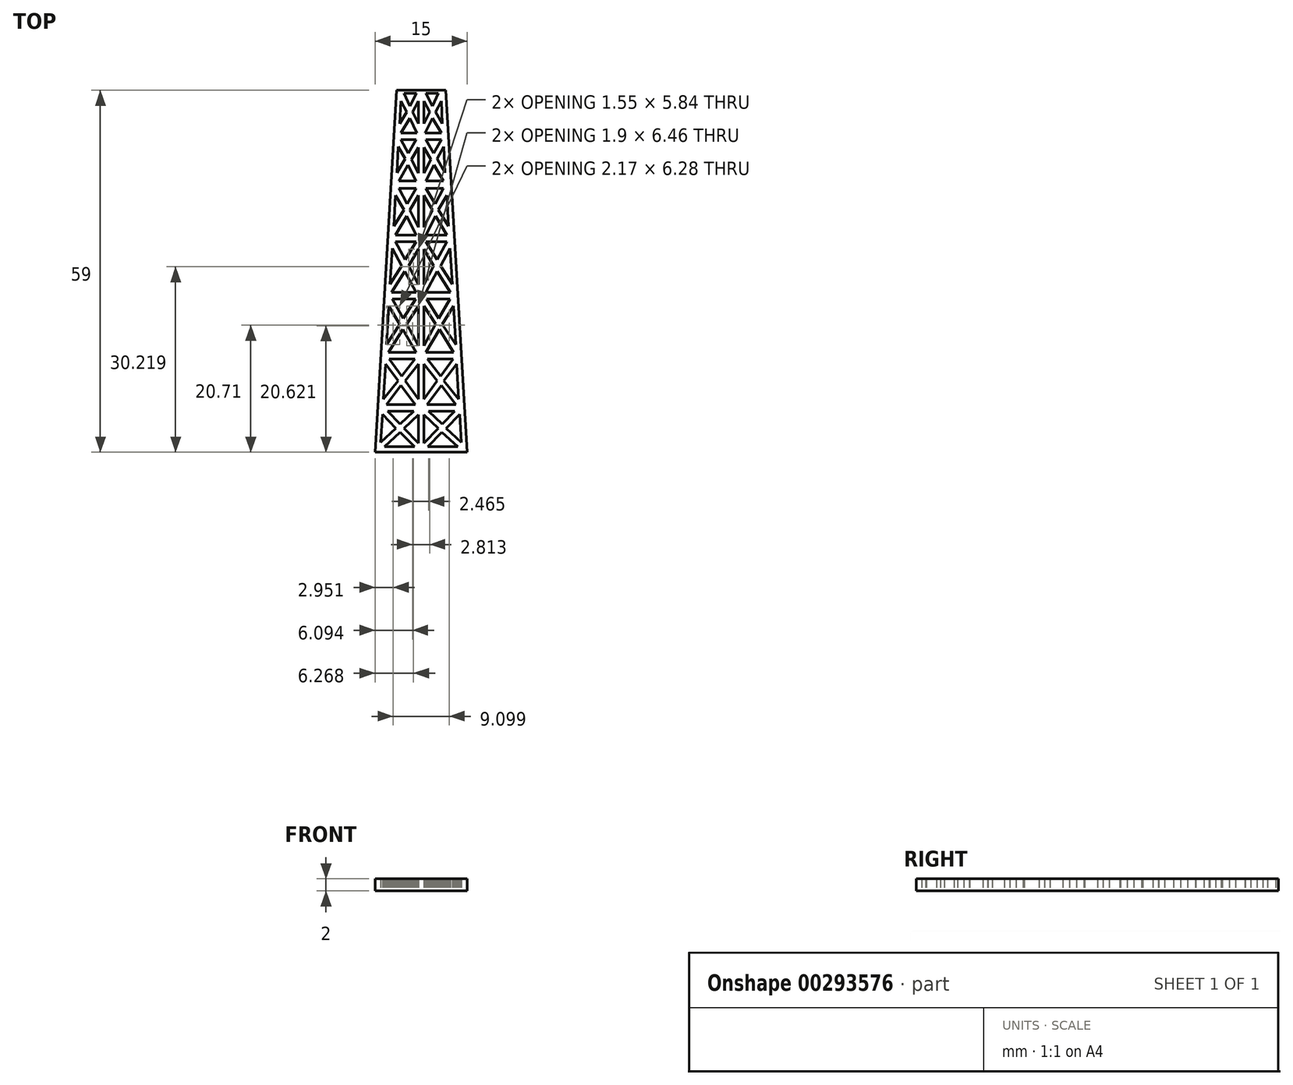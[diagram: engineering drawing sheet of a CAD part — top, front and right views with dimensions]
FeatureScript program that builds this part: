
annotation { "Feature Type Name" : "Feature", "Feature Type Description" : "" }
export const myFeature = defineFeature(function(context is Context, id is Id, definition is map)
    precondition{}
    {
        {
            var Q0;
            Q0=qCreatedBy(makeId("Top.planeOp"),FACE);
            var sketch = newSketch(context, id + "F0", { "sketchPlane" : qUnion([Q0])});
            skLineSegment(sketch, "E0", {"start": v(0, 25.75) * mm, "end": v(-4, 25.75) * mm});
            skLineSegment(sketch, "E1", {"start": v(-4, 25.75) * mm, "end": v(-7.5, -33.25) * mm});
            skLineSegment(sketch, "E2", {"start": v(-7.5, -33.25) * mm, "end": v(0, -33.25) * mm});
            skLineSegment(sketch, "E3", {"start": v(-2.81, 25.28) * mm, "end": v(-0.77, 25.28) * mm});
            skLineSegment(sketch, "E4", {"start": v(-0.77, 25.28) * mm, "end": v(-1.84, 23.18) * mm});
            skLineSegment(sketch, "E5", {"start": v(-1.84, 23.18) * mm, "end": v(-2.81, 25.28) * mm});
            skLineSegment(sketch, "E6", {"start": v(-0.45, 23.96) * mm, "end": v(-1.4, 22.21) * mm});
            skLineSegment(sketch, "E7", {"start": v(-1.4, 22.21) * mm, "end": v(-0.43, 20.28) * mm});
            skLineSegment(sketch, "E8", {"start": v(-0.43, 20.28) * mm, "end": v(-0.45, 23.96) * mm});
            skLineSegment(sketch, "E9", {"start": v(-3.29, 23.96) * mm, "end": v(-3.46, 20.3) * mm});
            skLineSegment(sketch, "E10", {"start": v(-3.46, 20.3) * mm, "end": v(-2.36, 22.21) * mm});
            skLineSegment(sketch, "E11", {"start": v(-2.36, 22.21) * mm, "end": v(-3.29, 23.96) * mm});
            skLineSegment(sketch, "E12", {"start": v(-3.29, 18.76) * mm, "end": v(-0.66, 18.76) * mm});
            skLineSegment(sketch, "E13", {"start": v(-0.66, 18.76) * mm, "end": v(-1.84, 21.21) * mm});
            skLineSegment(sketch, "E14", {"start": v(-1.84, 21.21) * mm, "end": v(-3.29, 18.76) * mm});
            skLineSegment(sketch, "E15", {"start": v(-3.29, 17.7) * mm, "end": v(-0.8, 17.7) * mm});
            skLineSegment(sketch, "E16", {"start": v(-0.8, 17.7) * mm, "end": v(-2.07, 15.47) * mm});
            skLineSegment(sketch, "E17", {"start": v(-2.07, 15.47) * mm, "end": v(-3.29, 17.7) * mm});
            skLineSegment(sketch, "E18", {"start": v(-1.57, 14.45) * mm, "end": v(-0.45, 16.4) * mm});
            skLineSegment(sketch, "E19", {"start": v(-0.45, 16.4) * mm, "end": v(-0.45, 12.22) * mm});
            skLineSegment(sketch, "E20", {"start": v(-0.45, 12.22) * mm, "end": v(-1.57, 14.45) * mm});
            skLineSegment(sketch, "E21", {"start": v(-3.72, 16.56) * mm, "end": v(-3.91, 12.3) * mm});
            skLineSegment(sketch, "E22", {"start": v(-3.91, 12.3) * mm, "end": v(-2.61, 14.57) * mm});
            skLineSegment(sketch, "E23", {"start": v(-2.61, 14.57) * mm, "end": v(-3.72, 16.56) * mm});
            skLineSegment(sketch, "E24", {"start": v(-3.64, 10.94) * mm, "end": v(-0.8, 10.94) * mm});
            skLineSegment(sketch, "E25", {"start": v(-0.8, 10.94) * mm, "end": v(-2.12, 13.58) * mm});
            skLineSegment(sketch, "E26", {"start": v(-2.12, 13.58) * mm, "end": v(-3.64, 10.94) * mm});
            skLineSegment(sketch, "E27", {"start": v(-3.64, 9.76) * mm, "end": v(-0.8, 9.76) * mm});
            skLineSegment(sketch, "E28", {"start": v(-0.8, 9.76) * mm, "end": v(-2.27, 7.2) * mm});
            skLineSegment(sketch, "E29", {"start": v(-2.27, 7.2) * mm, "end": v(-3.64, 9.76) * mm});
            skLineSegment(sketch, "E30", {"start": v(-0.45, 8.61) * mm, "end": v(-1.84, 6.18) * mm});
            skLineSegment(sketch, "E31", {"start": v(-1.84, 6.18) * mm, "end": v(-0.45, 3.41) * mm});
            skLineSegment(sketch, "E32", {"start": v(-0.45, 3.41) * mm, "end": v(-0.45, 8.61) * mm});
            skLineSegment(sketch, "E33", {"start": v(-4.17, 8.61) * mm, "end": v(-2.81, 6.25) * mm});
            skLineSegment(sketch, "E34", {"start": v(-2.81, 6.25) * mm, "end": v(-4.45, 3.62) * mm});
            skLineSegment(sketch, "E35", {"start": v(-4.45, 3.62) * mm, "end": v(-4.17, 8.61) * mm});
            skLineSegment(sketch, "E36", {"start": v(-4.17, 2.13) * mm, "end": v(-0.8, 2.13) * mm});
            skLineSegment(sketch, "E37", {"start": v(-0.8, 2.13) * mm, "end": v(-2.36, 5.25) * mm});
            skLineSegment(sketch, "E38", {"start": v(-2.36, 5.25) * mm, "end": v(-4.17, 2.13) * mm});
            skLineSegment(sketch, "E39", {"start": v(-4.17, 1.08) * mm, "end": v(-0.8, 1.08) * mm});
            skLineSegment(sketch, "E40", {"start": v(-0.8, 1.08) * mm, "end": v(-2.61, -1.83) * mm});
            skLineSegment(sketch, "E41", {"start": v(-2.61, -1.83) * mm, "end": v(-4.17, 1.08) * mm});
            skLineSegment(sketch, "E42", {"start": v(-0.45, -0.11) * mm, "end": v(-2, -2.84) * mm});
            skLineSegment(sketch, "E43", {"start": v(-2, -2.84) * mm, "end": v(-0.45, -5.95) * mm});
            skLineSegment(sketch, "E44", {"start": v(-0.45, -5.95) * mm, "end": v(-0.45, -0.11) * mm});
            skLineSegment(sketch, "E45", {"start": v(-4.71, 0) * mm, "end": v(-5.06, -5.83) * mm});
            skLineSegment(sketch, "E46", {"start": v(-5.06, -5.83) * mm, "end": v(-3.17, -2.84) * mm});
            skLineSegment(sketch, "E47", {"start": v(-3.17, -2.84) * mm, "end": v(-4.71, 0) * mm});
            skLineSegment(sketch, "E48", {"start": v(-4.79, -7.2) * mm, "end": v(-0.8, -7.2) * mm});
            skLineSegment(sketch, "E49", {"start": v(-0.8, -7.2) * mm, "end": v(-2.63, -3.76) * mm});
            skLineSegment(sketch, "E50", {"start": v(-2.63, -3.76) * mm, "end": v(-4.79, -7.2) * mm});
            skLineSegment(sketch, "E51", {"start": v(-4.71, -8.3) * mm, "end": v(-0.9, -8.3) * mm});
            skLineSegment(sketch, "E52", {"start": v(-0.9, -8.3) * mm, "end": v(-2.9, -11.46) * mm});
            skLineSegment(sketch, "E53", {"start": v(-2.9, -11.46) * mm, "end": v(-4.71, -8.3) * mm});
            skLineSegment(sketch, "E54", {"start": v(-0.45, -9.4) * mm, "end": v(-2.36, -12.36) * mm});
            skLineSegment(sketch, "E55", {"start": v(-2.36, -12.36) * mm, "end": v(-0.45, -15.86) * mm});
            skLineSegment(sketch, "E56", {"start": v(-0.45, -15.86) * mm, "end": v(-0.45, -9.4) * mm});
            skLineSegment(sketch, "E57", {"start": v(-5.63, -15.68) * mm, "end": v(-5.26, -9.4) * mm});
            skLineSegment(sketch, "E58", {"start": v(-5.26, -9.4) * mm, "end": v(-3.46, -12.37) * mm});
            skLineSegment(sketch, "E59", {"start": v(-3.46, -12.37) * mm, "end": v(-5.63, -15.68) * mm});
            skLineSegment(sketch, "E60", {"start": v(-5.3, -16.99) * mm, "end": v(-0.8, -16.99) * mm});
            skLineSegment(sketch, "E61", {"start": v(-0.8, -16.99) * mm, "end": v(-2.96, -13.25) * mm});
            skLineSegment(sketch, "E62", {"start": v(-2.96, -13.25) * mm, "end": v(-5.3, -16.99) * mm});
            skLineSegment(sketch, "E63", {"start": v(-5.2, -18.05) * mm, "end": v(-1, -18.05) * mm});
            skLineSegment(sketch, "E64", {"start": v(-1, -18.05) * mm, "end": v(-3.17, -20.85) * mm});
            skLineSegment(sketch, "E65", {"start": v(-3.17, -20.85) * mm, "end": v(-5.2, -18.05) * mm});
            skLineSegment(sketch, "E66", {"start": v(-0.45, -18.9) * mm, "end": v(-0.45, -24.6) * mm});
            skLineSegment(sketch, "E67", {"start": v(-0.45, -24.6) * mm, "end": v(-2.6, -21.62) * mm});
            skLineSegment(sketch, "E68", {"start": v(-2.6, -21.62) * mm, "end": v(-0.45, -18.9) * mm});
            skLineSegment(sketch, "E69", {"start": v(-5.8, -18.9) * mm, "end": v(-6.13, -24.57) * mm});
            skLineSegment(sketch, "E70", {"start": v(-6.13, -24.57) * mm, "end": v(-3.72, -21.6) * mm});
            skLineSegment(sketch, "E71", {"start": v(-3.72, -21.6) * mm, "end": v(-5.8, -18.9) * mm});
            skLineSegment(sketch, "E72", {"start": v(-3.29, -22.38) * mm, "end": v(-5.63, -25.5) * mm});
            skLineSegment(sketch, "E73", {"start": v(-5.63, -25.5) * mm, "end": v(-0.96, -25.5) * mm});
            skLineSegment(sketch, "E74", {"start": v(-0.96, -25.5) * mm, "end": v(-3.29, -22.38) * mm});
            skLineSegment(sketch, "E75", {"start": v(-5.45, -26.56) * mm, "end": v(-1.23, -26.56) * mm});
            skLineSegment(sketch, "E76", {"start": v(-1.23, -26.56) * mm, "end": v(-3.4, -28.68) * mm});
            skLineSegment(sketch, "E77", {"start": v(-3.4, -28.68) * mm, "end": v(-5.45, -26.56) * mm});
            skLineSegment(sketch, "E78", {"start": v(-2.81, -29.33) * mm, "end": v(-0.45, -31.73) * mm});
            skLineSegment(sketch, "E79", {"start": v(-0.45, -31.73) * mm, "end": v(-0.45, -27.1) * mm});
            skLineSegment(sketch, "E80", {"start": v(-0.45, -27.1) * mm, "end": v(-2.81, -29.33) * mm});
            skLineSegment(sketch, "E81", {"start": v(-6.57, -31.64) * mm, "end": v(-4.09, -29.33) * mm});
            skLineSegment(sketch, "E82", {"start": v(-4.09, -29.33) * mm, "end": v(-6.3, -27.08) * mm});
            skLineSegment(sketch, "E83", {"start": v(-6.3, -27.08) * mm, "end": v(-6.57, -31.64) * mm});
            skLineSegment(sketch, "E84", {"start": v(-5.97, -32.35) * mm, "end": v(-1.07, -32.35) * mm});
            skLineSegment(sketch, "E85", {"start": v(-1.07, -32.35) * mm, "end": v(-3.4, -29.98) * mm});
            skLineSegment(sketch, "E86", {"start": v(-3.4, -29.98) * mm, "end": v(-5.97, -32.35) * mm});
            skLineSegment(sketch, "E87.MirrorCS", {"start": v(0, 25.75) * mm, "end": v(4, 25.75) * mm});
            skLineSegment(sketch, "E88.MirrorCS", {"start": v(4, 25.75) * mm, "end": v(7.5, -33.25) * mm});
            skLineSegment(sketch, "E89.MirrorCS", {"start": v(2.81, 25.28) * mm, "end": v(0.77, 25.28) * mm});
            skLineSegment(sketch, "E90.MirrorCS", {"start": v(1.84, 23.18) * mm, "end": v(2.81, 25.28) * mm});
            skLineSegment(sketch, "E91.MirrorCS", {"start": v(2.36, 22.21) * mm, "end": v(3.29, 23.96) * mm});
            skLineSegment(sketch, "E92.MirrorCS", {"start": v(3.29, 23.96) * mm, "end": v(3.46, 20.3) * mm});
            skLineSegment(sketch, "E93.MirrorCS", {"start": v(3.46, 20.3) * mm, "end": v(2.36, 22.21) * mm});
            skLineSegment(sketch, "E94.MirrorCS", {"start": v(1.84, 21.21) * mm, "end": v(3.29, 18.76) * mm});
            skLineSegment(sketch, "E95.MirrorCS", {"start": v(3.29, 18.76) * mm, "end": v(0.66, 18.76) * mm});
            skLineSegment(sketch, "E96.MirrorCS", {"start": v(0.66, 18.76) * mm, "end": v(1.84, 21.21) * mm});
            skLineSegment(sketch, "E97.MirrorCS", {"start": v(1.4, 22.21) * mm, "end": v(0.43, 20.28) * mm});
            skLineSegment(sketch, "E98.MirrorCS", {"start": v(0.45, 23.96) * mm, "end": v(1.4, 22.21) * mm});
            skLineSegment(sketch, "E99.MirrorCS", {"start": v(0.77, 25.28) * mm, "end": v(1.84, 23.18) * mm});
            skLineSegment(sketch, "E100.MirrorCS", {"start": v(3.29, 17.7) * mm, "end": v(0.8, 17.7) * mm});
            skLineSegment(sketch, "E101.MirrorCS", {"start": v(2.07, 15.47) * mm, "end": v(3.29, 17.7) * mm});
            skLineSegment(sketch, "E102.MirrorCS", {"start": v(2.61, 14.57) * mm, "end": v(3.72, 16.56) * mm});
            skLineSegment(sketch, "E103.MirrorCS", {"start": v(3.72, 16.56) * mm, "end": v(3.91, 12.3) * mm});
            skLineSegment(sketch, "E104.MirrorCS", {"start": v(3.91, 12.3) * mm, "end": v(2.61, 14.57) * mm});
            skLineSegment(sketch, "E105.MirrorCS", {"start": v(2.12, 13.58) * mm, "end": v(3.64, 10.94) * mm});
            skLineSegment(sketch, "E106.MirrorCS", {"start": v(3.64, 10.94) * mm, "end": v(0.8, 10.94) * mm});
            skLineSegment(sketch, "E107.MirrorCS", {"start": v(0.8, 10.94) * mm, "end": v(2.12, 13.58) * mm});
            skLineSegment(sketch, "E108.MirrorCS", {"start": v(0.45, 12.22) * mm, "end": v(1.57, 14.45) * mm});
            skLineSegment(sketch, "E109.MirrorCS", {"start": v(0.45, 16.4) * mm, "end": v(0.45, 12.22) * mm});
            skLineSegment(sketch, "E110.MirrorCS", {"start": v(1.57, 14.45) * mm, "end": v(0.45, 16.4) * mm});
            skLineSegment(sketch, "E111.MirrorCS", {"start": v(0.8, 17.7) * mm, "end": v(2.07, 15.47) * mm});
            skLineSegment(sketch, "E112.MirrorCS", {"start": v(0.8, 9.76) * mm, "end": v(2.27, 7.2) * mm});
            skLineSegment(sketch, "E113.MirrorCS", {"start": v(3.64, 9.76) * mm, "end": v(0.8, 9.76) * mm});
            skLineSegment(sketch, "E114.MirrorCS", {"start": v(2.27, 7.2) * mm, "end": v(3.64, 9.76) * mm});
            skLineSegment(sketch, "E115.MirrorCS", {"start": v(4.17, 8.61) * mm, "end": v(2.81, 6.25) * mm});
            skLineSegment(sketch, "E116.MirrorCS", {"start": v(4.45, 3.62) * mm, "end": v(4.17, 8.61) * mm});
            skLineSegment(sketch, "E117.MirrorCS", {"start": v(2.81, 6.25) * mm, "end": v(4.45, 3.62) * mm});
            skLineSegment(sketch, "E118.MirrorCS", {"start": v(2.36, 5.25) * mm, "end": v(4.17, 2.13) * mm});
            skLineSegment(sketch, "E119.MirrorCS", {"start": v(4.17, 2.13) * mm, "end": v(0.8, 2.13) * mm});
            skLineSegment(sketch, "E120.MirrorCS", {"start": v(0.8, 2.13) * mm, "end": v(2.36, 5.25) * mm});
            skLineSegment(sketch, "E121.MirrorCS", {"start": v(1.84, 6.18) * mm, "end": v(0.45, 3.41) * mm});
            skLineSegment(sketch, "E122.MirrorCS", {"start": v(0.45, 3.41) * mm, "end": v(0.45, 8.61) * mm});
            skLineSegment(sketch, "E123.MirrorCS", {"start": v(0.45, 8.61) * mm, "end": v(1.84, 6.18) * mm});
            skLineSegment(sketch, "E124.MirrorCS", {"start": v(4.17, 1.08) * mm, "end": v(0.8, 1.08) * mm});
            skLineSegment(sketch, "E125.MirrorCS", {"start": v(2.61, -1.83) * mm, "end": v(4.17, 1.08) * mm});
            skLineSegment(sketch, "E126.MirrorCS", {"start": v(0.8, 1.08) * mm, "end": v(2.61, -1.83) * mm});
            skLineSegment(sketch, "E127.MirrorCS", {"start": v(0.45, -0.11) * mm, "end": v(2, -2.84) * mm});
            skLineSegment(sketch, "E128.MirrorCS", {"start": v(0.45, -5.95) * mm, "end": v(0.45, -0.11) * mm});
            skLineSegment(sketch, "E129.MirrorCS", {"start": v(2, -2.84) * mm, "end": v(0.45, -5.95) * mm});
            skLineSegment(sketch, "E130.MirrorCS", {"start": v(0.8, -7.2) * mm, "end": v(2.63, -3.76) * mm});
            skLineSegment(sketch, "E131.MirrorCS", {"start": v(4.79, -7.2) * mm, "end": v(0.8, -7.2) * mm});
            skLineSegment(sketch, "E132.MirrorCS", {"start": v(2.63, -3.76) * mm, "end": v(4.79, -7.2) * mm});
            skLineSegment(sketch, "E133.MirrorCS", {"start": v(5.06, -5.83) * mm, "end": v(3.17, -2.84) * mm});
            skLineSegment(sketch, "E134.MirrorCS", {"start": v(4.71, 0) * mm, "end": v(5.06, -5.83) * mm});
            skLineSegment(sketch, "E135.MirrorCS", {"start": v(3.17, -2.84) * mm, "end": v(4.71, 0) * mm});
            skLineSegment(sketch, "E136.MirrorCS", {"start": v(4.71, -8.3) * mm, "end": v(0.9, -8.3) * mm});
            skLineSegment(sketch, "E137.MirrorCS", {"start": v(0.9, -8.3) * mm, "end": v(2.9, -11.46) * mm});
            skLineSegment(sketch, "E138.MirrorCS", {"start": v(2.9, -11.46) * mm, "end": v(4.71, -8.3) * mm});
            skLineSegment(sketch, "E139.MirrorCS", {"start": v(5.26, -9.4) * mm, "end": v(3.46, -12.37) * mm});
            skLineSegment(sketch, "E140.MirrorCS", {"start": v(5.63, -15.68) * mm, "end": v(5.26, -9.4) * mm});
            skLineSegment(sketch, "E141.MirrorCS", {"start": v(3.46, -12.37) * mm, "end": v(5.63, -15.68) * mm});
            skLineSegment(sketch, "E142.MirrorCS", {"start": v(2.96, -13.25) * mm, "end": v(5.3, -16.99) * mm});
            skLineSegment(sketch, "E143.MirrorCS", {"start": v(0.8, -16.99) * mm, "end": v(2.96, -13.25) * mm});
            skLineSegment(sketch, "E144.MirrorCS", {"start": v(5.3, -16.99) * mm, "end": v(0.8, -16.99) * mm});
            skLineSegment(sketch, "E145.MirrorCS", {"start": v(0.45, -15.86) * mm, "end": v(0.45, -9.4) * mm});
            skLineSegment(sketch, "E146.MirrorCS", {"start": v(2.36, -12.36) * mm, "end": v(0.45, -15.86) * mm});
            skLineSegment(sketch, "E147.MirrorCS", {"start": v(0.45, -9.4) * mm, "end": v(2.36, -12.36) * mm});
            skLineSegment(sketch, "E148.MirrorCS", {"start": v(5.63, -25.5) * mm, "end": v(0.96, -25.5) * mm});
            skLineSegment(sketch, "E149.MirrorCS", {"start": v(0.96, -25.5) * mm, "end": v(3.29, -22.38) * mm});
            skLineSegment(sketch, "E150.MirrorCS", {"start": v(3.29, -22.38) * mm, "end": v(5.63, -25.5) * mm});
            skLineSegment(sketch, "E151.MirrorCS", {"start": v(6.13, -24.57) * mm, "end": v(3.72, -21.6) * mm});
            skLineSegment(sketch, "E152.MirrorCS", {"start": v(5.8, -18.9) * mm, "end": v(6.13, -24.57) * mm});
            skLineSegment(sketch, "E153.MirrorCS", {"start": v(3.72, -21.6) * mm, "end": v(5.8, -18.9) * mm});
            skLineSegment(sketch, "E154.MirrorCS", {"start": v(5.2, -18.05) * mm, "end": v(1, -18.05) * mm});
            skLineSegment(sketch, "E155.MirrorCS", {"start": v(1, -18.05) * mm, "end": v(3.17, -20.85) * mm});
            skLineSegment(sketch, "E156.MirrorCS", {"start": v(2.6, -21.62) * mm, "end": v(0.45, -18.9) * mm});
            skLineSegment(sketch, "E157.MirrorCS", {"start": v(0.45, -18.9) * mm, "end": v(0.45, -24.6) * mm});
            skLineSegment(sketch, "E158.MirrorCS", {"start": v(0.45, -24.6) * mm, "end": v(2.6, -21.62) * mm});
            skLineSegment(sketch, "E159.MirrorCS", {"start": v(3.17, -20.85) * mm, "end": v(5.2, -18.05) * mm});
            skLineSegment(sketch, "E160.MirrorCS", {"start": v(0.45, -31.73) * mm, "end": v(0.45, -27.1) * mm});
            skLineSegment(sketch, "E161.MirrorCS", {"start": v(2.81, -29.33) * mm, "end": v(0.45, -31.73) * mm});
            skLineSegment(sketch, "E162.MirrorCS", {"start": v(1.07, -32.35) * mm, "end": v(3.4, -29.98) * mm});
            skLineSegment(sketch, "E163.MirrorCS", {"start": v(5.97, -32.35) * mm, "end": v(1.07, -32.35) * mm});
            skLineSegment(sketch, "E164.MirrorCS", {"start": v(3.4, -29.98) * mm, "end": v(5.97, -32.35) * mm});
            skLineSegment(sketch, "E165.MirrorCS", {"start": v(6.57, -31.64) * mm, "end": v(4.09, -29.33) * mm});
            skLineSegment(sketch, "E166.MirrorCS", {"start": v(6.3, -27.08) * mm, "end": v(6.57, -31.64) * mm});
            skLineSegment(sketch, "E167.MirrorCS", {"start": v(4.09, -29.33) * mm, "end": v(6.3, -27.08) * mm});
            skLineSegment(sketch, "E168.MirrorCS", {"start": v(3.4, -28.68) * mm, "end": v(5.45, -26.56) * mm});
            skLineSegment(sketch, "E169.MirrorCS", {"start": v(5.45, -26.56) * mm, "end": v(1.23, -26.56) * mm});
            skLineSegment(sketch, "E170.MirrorCS", {"start": v(1.23, -26.56) * mm, "end": v(3.4, -28.68) * mm});
            skLineSegment(sketch, "E171.MirrorCS", {"start": v(0.45, -27.1) * mm, "end": v(2.81, -29.33) * mm});
            skLineSegment(sketch, "E172.MirrorCS", {"start": v(7.5, -33.25) * mm, "end": v(0, -33.25) * mm});
            skLineSegment(sketch, "E173.MirrorCS", {"start": v(0.43, 20.28) * mm, "end": v(0.45, 23.96) * mm});
            skSolve(sketch);
        }
        {
            var Q0;
            Q0=makeQuery(id+"F0.imprint","IMPRINT",FACE,{"disambiguationData":[TD([[makeQuery(id+"F0.imprint","IMPRINT",EDGE,{"derivedFrom":sQuery(id+"F0.wireOp",EDGE,"E0")}),1.0]])]});
            extrude(context, id + "F1", {"entities" : qUnion([Q0]), "offsetDistance" : 25 * mm, "depth" : 2 * mm});
        }
    });
